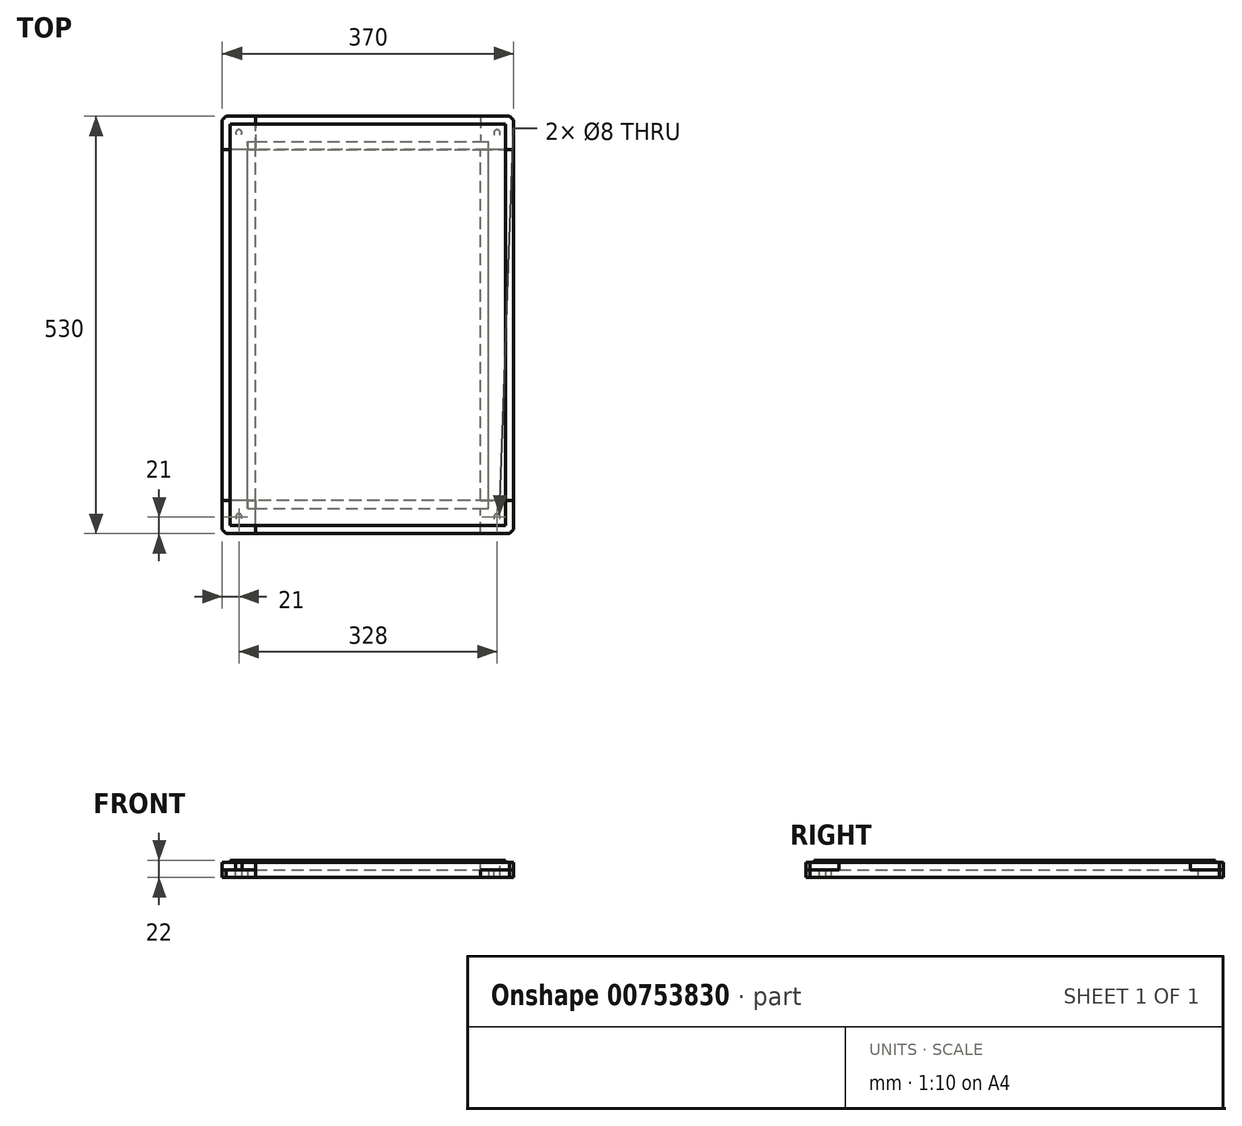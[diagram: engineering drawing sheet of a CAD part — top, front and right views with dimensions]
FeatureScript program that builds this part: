
annotation { "Feature Type Name" : "Feature", "Feature Type Description" : "" }
export const myFeature = defineFeature(function(context is Context, id is Id, definition is map)
    precondition{}
    {
        {
            assignVariable(context, id + "F0", {"name" : "Glass_Thickness", "anyValue" : 3});
        }
        {
            assignVariable(context, id + "F1", {"name" : "Frame_Thickness", "anyValue" : 19});
        }
        {
            assignVariable(context, id + "F2", {"name" : "Rebate_Depth", "anyValue" : 10});
        }
        {
            var Q0;
            Q0=qCreatedBy(makeId("Top.planeOp"),FACE);
            var sketch = newSketch(context, id + "F3", { "sketchPlane" : qUnion([Q0])});
            skLineSegment(sketch, "E0.bottom", {"start": v(-175, 255) * mm, "end": v(175, 255) * mm});
            skLineSegment(sketch, "E0.top", {"start": v(-175, -255) * mm, "end": v(175, -255) * mm});
            skLineSegment(sketch, "E0.left", {"start": v(-175, 255) * mm, "end": v(-175, -255) * mm});
            skLineSegment(sketch, "E0.right", {"start": v(175, 255) * mm, "end": v(175, -255) * mm});
            skSolve(sketch);
        }
        {
            var Q0;
            Q0=makeQuery(id+"F3.imprint","IMPRINT",FACE,{"disambiguationData":[TD([[makeQuery(id+"F3.imprint","IMPRINT",EDGE,{"derivedFrom":sQuery(id+"F3.wireOp",EDGE,"E0.bottom")}),-1.0]])]});
            extrude(context, id + "F4", {"entities" : qUnion([Q0]), "depth" : (getVariable(context, 'Glass_Thickness')) * mm, "offsetDistance" : 25 * mm});
        }
        {
            var Q0;
            Q0=makeQuery(id+"F4.opExtrude","CAP_FACE",FACE,{"disambiguationData":[OSD([sQuery(id+"F3.wireOp",EDGE,"E0.bottom"),sQuery(id+"F3.wireOp",EDGE,"E0.top"),sQuery(id+"F3.wireOp",EDGE,"E0.left"),sQuery(id+"F3.wireOp",EDGE,"E0.right")])],"isStart":true});
            var sketch = newSketch(context, id + "F5", { "sketchPlane" : qUnion([Q0])});
            skLineSegment(sketch, "E1.bottom", {"start": v(185, -265) * mm, "end": v(-185, -265) * mm});
            skLineSegment(sketch, "E1.top", {"start": v(185, -223) * mm, "end": v(-185, -223) * mm});
            skLineSegment(sketch, "E1.left", {"start": v(185, -265) * mm, "end": v(185, -223) * mm});
            skLineSegment(sketch, "E1.right", {"start": v(-185, -265) * mm, "end": v(-185, -223) * mm});
            skCircle(sketch, "E2", {"center": v(-164, -244) * mm, "radius": 4 * mm});
            skCircle(sketch, "E3.MirrorC", {"center": v(164, -244) * mm, "radius": 4 * mm});
            skSolve(sketch);
        }
        {
            var Q0;
            Q0=makeQuery(id+"F5.imprint","IMPRINT",FACE,{"disambiguationData":[TD([[makeQuery(id+"F5.imprint","IMPRINT",EDGE,{"derivedFrom":sQuery(id+"F5.wireOp",EDGE,"E1.bottom")}),-1.0]])]});
            var Q1;
            {var subQ1=makeQuery(id+"F4.opExtrude","CAP_EDGE",EDGE,{"disambiguationData":[OSD([sQuery(id+"F3.wireOp",EDGE,"E0.right")])],"isStart":true});var subQ5=sQuery(id+"F5.wireOp",EDGE,"E1.top");var subQ6=makeQuery(id+"F5.imprint","INTERSECT",VERTEX,{"derivedFrom":[subQ1,subQ5]});Q1=makeQuery(id+"F5.imprint","IMPRINT",FACE,{"disambiguationData":[TD([[makeQuery(id+"F5.imprint","IMPRINT",EDGE,{"disambiguationData":[TD([[subQ6,-1.0]])],"derivedFrom":subQ5}),1.0]])]});}
            var Q2;
            {var subQ0=sQuery(id+"F5.wireOp",EDGE,"E3.MirrorC");var subQ1=makeQuery(id+"F4.opExtrude","CAP_EDGE",EDGE,{"disambiguationData":[OSD([sQuery(id+"F3.wireOp",EDGE,"E0.bottom")])],"isStart":true});var subQ2=makeQuery(id+"F5.imprint","INTERSECT",VERTEX,{"derivedFrom":[subQ1,subQ0]});Q2=makeQuery(id+"F5.imprint","IMPRINT",FACE,{"disambiguationData":[TD([[makeQuery(id+"F5.imprint","IMPRINT",EDGE,{"disambiguationData":[TD([[subQ2,1.0]])],"derivedFrom":subQ0}),1.0]])]});}
            var Q3;
            {var subQ0=sQuery(id+"F5.wireOp",EDGE,"E2");var subQ1=makeQuery(id+"F4.opExtrude","CAP_EDGE",EDGE,{"disambiguationData":[OSD([sQuery(id+"F3.wireOp",EDGE,"E0.bottom")])],"isStart":true});var subQ2=makeQuery(id+"F5.imprint","INTERSECT",VERTEX,{"derivedFrom":[subQ1,subQ0]});Q3=makeQuery(id+"F5.imprint","IMPRINT",FACE,{"disambiguationData":[TD([[makeQuery(id+"F5.imprint","IMPRINT",EDGE,{"disambiguationData":[TD([[subQ2,1.0]])],"derivedFrom":subQ0}),-1.0]])]});}
            extrude(context, id + "F6", {"entities" : qUnion([Q0, Q1, Q2, Q3]), "depth" : (getVariable(context, 'Frame_Thickness')) * mm, "offsetDistance" : 25 * mm});
        }
        {
            var Q0;
            Q0=makeQuery(id+"F6.opExtrude","CAP_FACE",FACE,{"disambiguationData":[OSD([sQuery(id+"F5.wireOp",EDGE,"E1.bottom"),sQuery(id+"F5.wireOp",EDGE,"E1.top"),sQuery(id+"F5.wireOp",EDGE,"E1.left"),sQuery(id+"F5.wireOp",EDGE,"E1.right"),sQuery(id+"F5.wireOp",EDGE,"E2"),sQuery(id+"F5.wireOp",EDGE,"E3.MirrorC")])],"isStart":false});
            var sketch = newSketch(context, id + "F7", { "sketchPlane" : qUnion([Q0])});
            skLineSegment(sketch, "E4", {"start": v(143, -265) * mm, "end": v(143, -223) * mm});
            skLineSegment(sketch, "E5.MirrorCS", {"start": v(-143, -265) * mm, "end": v(-143, -223) * mm});
            skSolve(sketch);
        }
        {
            var Q0;
            {var subQ2=sQuery(id+"F7.wireOp",EDGE,"E5.MirrorCS");Q0=makeQuery(id+"F7.imprint","IMPRINT",FACE,{"disambiguationData":[TD([[makeQuery(id+"F7.imprint","IMPRINT",EDGE,{"derivedFrom":subQ2}),1.0]])]});}
            var Q1;
            {var subQ2=sQuery(id+"F7.wireOp",EDGE,"E4");Q1=makeQuery(id+"F7.imprint","IMPRINT",FACE,{"disambiguationData":[TD([[makeQuery(id+"F7.imprint","IMPRINT",EDGE,{"derivedFrom":subQ2}),-1.0]])]});}
            extrude(context, id + "F8", {"entities" : qUnion([Q0, Q1]), "operationType" : NewBodyOperationType.REMOVE, "oppositeDirection" : true, "depth" : (getVariable(context, 'Frame_Thickness') / 2) * mm, "offsetDistance" : 25 * mm});
        }
        {
            var Q0;
            Q0=makeQuery(id+"F6.opExtrude","SWEPT_EDGE",EDGE,{"disambiguationData":[OSD([sQuery(id+"F5.wireOp",EDGE,"E1.bottom"),sQuery(id+"F5.wireOp",EDGE,"E1.right")])]});
            var Q1;
            Q1=makeQuery(id+"F6.opExtrude","SWEPT_EDGE",EDGE,{"disambiguationData":[OSD([sQuery(id+"F5.wireOp",EDGE,"E1.bottom"),sQuery(id+"F5.wireOp",EDGE,"E1.left")])]});
            chamfer(context, id + "F9", {"entities" : qUnion([Q0, Q1]), "width" : 5 * mm, "tangentPropagation" : true});
        }
        {
            var Q0;
            Q0=makeQuery(id+"F6.opExtrude","SWEPT_BODY",BODY,{"disambiguationData":[OSD([sQuery(id+"F5.wireOp",EDGE,"E1.bottom"),sQuery(id+"F5.wireOp",EDGE,"E1.top"),sQuery(id+"F5.wireOp",EDGE,"E1.left"),sQuery(id+"F5.wireOp",EDGE,"E1.right"),sQuery(id+"F5.wireOp",EDGE,"E2"),sQuery(id+"F5.wireOp",EDGE,"E3.MirrorC")])]});
            var Q1;
            Q1=qCreatedBy(makeId("Front.planeOp"),FACE);
            mirror(context, id + "F10", {"operationType" : NewBodyOperationType.ADD, "entities" : qUnion([Q0]), "mirrorPlane" : qUnion([Q1])});
        }
        {
            var Q0;
            Q0=makeQuery(id+"F4.opExtrude","CAP_FACE",FACE,{"disambiguationData":[OSD([sQuery(id+"F3.wireOp",EDGE,"E0.bottom"),sQuery(id+"F3.wireOp",EDGE,"E0.top"),sQuery(id+"F3.wireOp",EDGE,"E0.left"),sQuery(id+"F3.wireOp",EDGE,"E0.right")])],"isStart":true});
            var sketch = newSketch(context, id + "F11", { "sketchPlane" : qUnion([Q0])});
            skLineSegment(sketch, "E6.bottom", {"start": v(-185, 265) * mm, "end": v(-143, 265) * mm});
            skLineSegment(sketch, "E6.top", {"start": v(-185, -265) * mm, "end": v(-143, -265) * mm});
            skLineSegment(sketch, "E6.left", {"start": v(-185, 265) * mm, "end": v(-185, -265) * mm});
            skLineSegment(sketch, "E6.right", {"start": v(-143, 265) * mm, "end": v(-143, -265) * mm});
            skCircle(sketch, "E7", {"center": v(-164, 244) * mm, "radius": 4 * mm});
            skCircle(sketch, "E8.MirrorC", {"center": v(-164, -244) * mm, "radius": 4 * mm});
            skSolve(sketch);
        }
        {
            var Q0;
            {var subQ13=sQuery(id+"F11.wireOp",EDGE,"E6.bottom");Q0=makeQuery(id+"F11.imprint","IMPRINT",FACE,{"disambiguationData":[TD([[makeQuery(id+"F11.imprint","IMPRINT",EDGE,{"derivedFrom":subQ13}),-1.0]])]});}
            var Q1;
            {var subQ0=sQuery(id+"F11.wireOp",EDGE,"E8.MirrorC");var subQ1=makeQuery(id+"F4.opExtrude","CAP_EDGE",EDGE,{"disambiguationData":[OSD([sQuery(id+"F3.wireOp",EDGE,"E0.bottom")])],"isStart":true});var subQ2=makeQuery(id+"F11.imprint","INTERSECT",VERTEX,{"derivedFrom":[subQ1,subQ0]});Q1=makeQuery(id+"F11.imprint","IMPRINT",FACE,{"disambiguationData":[TD([[makeQuery(id+"F11.imprint","IMPRINT",EDGE,{"disambiguationData":[TD([[subQ2,-1.0]])],"derivedFrom":subQ0}),1.0]])]});}
            var Q2;
            {var subQ0=sQuery(id+"F11.wireOp",EDGE,"E6.right");var subQ6=makeQuery(id+"F4.opExtrude","CAP_EDGE",EDGE,{"disambiguationData":[OSD([sQuery(id+"F3.wireOp",EDGE,"E0.top")])],"isStart":true});var subQ11=makeQuery(id+"F11.imprint","INTERSECT",VERTEX,{"derivedFrom":[subQ6,subQ0]});Q2=makeQuery(id+"F11.imprint","IMPRINT",FACE,{"disambiguationData":[TD([[makeQuery(id+"F11.imprint","IMPRINT",EDGE,{"disambiguationData":[TD([[subQ11,-1.0]])],"derivedFrom":subQ0}),-1.0]])]});}
            var Q3;
            {var subQ0=sQuery(id+"F11.wireOp",EDGE,"E7");var subQ1=makeQuery(id+"F4.opExtrude","CAP_EDGE",EDGE,{"disambiguationData":[OSD([sQuery(id+"F3.wireOp",EDGE,"E0.top")])],"isStart":true});var subQ2=makeQuery(id+"F11.imprint","INTERSECT",VERTEX,{"derivedFrom":[subQ1,subQ0]});Q3=makeQuery(id+"F11.imprint","IMPRINT",FACE,{"disambiguationData":[TD([[makeQuery(id+"F11.imprint","IMPRINT",EDGE,{"disambiguationData":[TD([[subQ2,-1.0]])],"derivedFrom":subQ0}),-1.0]])]});}
            extrude(context, id + "F12", {"entities" : qUnion([Q0, Q1, Q2, Q3]), "depth" : (getVariable(context, 'Frame_Thickness')) * mm, "offsetDistance" : 25 * mm});
        }
        {
            var Q0;
            Q0=makeQuery(id+"F12.opExtrude","CAP_FACE",FACE,{"disambiguationData":[OSD([sQuery(id+"F11.wireOp",EDGE,"E6.bottom"),sQuery(id+"F11.wireOp",EDGE,"E6.top"),sQuery(id+"F11.wireOp",EDGE,"E6.left"),sQuery(id+"F11.wireOp",EDGE,"E6.right"),sQuery(id+"F11.wireOp",EDGE,"E7"),sQuery(id+"F11.wireOp",EDGE,"E8.MirrorC")])],"isStart":true});
            var sketch = newSketch(context, id + "F13", { "sketchPlane" : qUnion([Q0])});
            skLineSegment(sketch, "E9", {"start": v(-143, -223) * mm, "end": v(-185, -223) * mm});
            skLineSegment(sketch, "E10.MirrorCS", {"start": v(-143, 223) * mm, "end": v(-185, 223) * mm});
            skSolve(sketch);
        }
        {
            var Q0;
            {var subQ2=sQuery(id+"F13.wireOp",EDGE,"E10.MirrorCS");Q0=makeQuery(id+"F13.imprint","IMPRINT",FACE,{"disambiguationData":[TD([[makeQuery(id+"F13.imprint","IMPRINT",EDGE,{"derivedFrom":subQ2}),-1.0]])]});}
            var Q1;
            {var subQ2=sQuery(id+"F13.wireOp",EDGE,"E9");Q1=makeQuery(id+"F13.imprint","IMPRINT",FACE,{"disambiguationData":[TD([[makeQuery(id+"F13.imprint","IMPRINT",EDGE,{"derivedFrom":subQ2}),1.0]])]});}
            extrude(context, id + "F14", {"entities" : qUnion([Q0, Q1]), "operationType" : NewBodyOperationType.REMOVE, "oppositeDirection" : true, "depth" : (getVariable(context, 'Frame_Thickness') / 2) * mm, "offsetDistance" : 25 * mm});
        }
        {
            var Q0;
            Q0=makeQuery(id+"F12.opExtrude","SWEPT_EDGE",EDGE,{"disambiguationData":[OSD([sQuery(id+"F11.wireOp",EDGE,"E6.bottom"),sQuery(id+"F11.wireOp",EDGE,"E6.left")])]});
            var Q1;
            Q1=makeQuery(id+"F12.opExtrude","SWEPT_EDGE",EDGE,{"disambiguationData":[OSD([sQuery(id+"F11.wireOp",EDGE,"E6.top"),sQuery(id+"F11.wireOp",EDGE,"E6.left")])]});
            chamfer(context, id + "F15", {"entities" : qUnion([Q0, Q1]), "width" : 5 * mm, "tangentPropagation" : true});
        }
        {
            var Q0;
            Q0=makeQuery(id+"F12.opExtrude","SWEPT_BODY",BODY,{"disambiguationData":[OSD([sQuery(id+"F11.wireOp",EDGE,"E6.bottom"),sQuery(id+"F11.wireOp",EDGE,"E6.top"),sQuery(id+"F11.wireOp",EDGE,"E6.left"),sQuery(id+"F11.wireOp",EDGE,"E6.right"),sQuery(id+"F11.wireOp",EDGE,"E7"),sQuery(id+"F11.wireOp",EDGE,"E8.MirrorC")])]});
            var Q1;
            Q1=qCreatedBy(makeId("Right.planeOp"),FACE);
            mirror(context, id + "F16", {"entities" : qUnion([Q0]), "mirrorPlane" : qUnion([Q1])});
        }
        {
            var Q0;
            Q0=makeQuery(id+"F4.opExtrude","CAP_FACE",FACE,{"disambiguationData":[OSD([sQuery(id+"F3.wireOp",EDGE,"E0.bottom"),sQuery(id+"F3.wireOp",EDGE,"E0.top"),sQuery(id+"F3.wireOp",EDGE,"E0.left"),sQuery(id+"F3.wireOp",EDGE,"E0.right")])],"isStart":true});
            var sketch = newSketch(context, id + "F17", { "sketchPlane" : qUnion([Q0])});
            skCircle(sketch, "E11.0", {"center": v(-164, 244) * mm, "radius": 4 * mm});
            skCircle(sketch, "E12.0", {"center": v(164, 244) * mm, "radius": 4 * mm});
            skCircle(sketch, "E13.0", {"center": v(164, -244) * mm, "radius": 4 * mm});
            skCircle(sketch, "E14.0", {"center": v(-164, -244) * mm, "radius": 4 * mm});
            skSolve(sketch);
        }
        {
            var Q0;
            {var subQ0=sQuery(id+"F17.wireOp",EDGE,"E11.0");var subQ1=makeQuery(id+"F17.imprint","INTERSECT",VERTEX,{"derivedFrom":[makeQuery(id+"F4.opExtrude","CAP_EDGE",EDGE,{"disambiguationData":[OSD([sQuery(id+"F3.wireOp",EDGE,"E0.top")])],"isStart":true}),subQ0]});Q0=makeQuery(id+"F17.imprint","IMPRINT",FACE,{"disambiguationData":[TD([[makeQuery(id+"F17.imprint","IMPRINT",EDGE,{"disambiguationData":[TD([[subQ1,-1.0]])],"derivedFrom":subQ0}),1.0]])]});}
            extrude(context, id + "F18", {"entities" : qUnion([Q0]), "depth" : (getVariable(context, 'Frame_Thickness')) * mm, "offsetDistance" : 25 * mm});
        }
        {
            var Q0;
            Q0=makeQuery(id+"F18.opExtrude","SWEPT_BODY",BODY,{"disambiguationData":[OSD([sQuery(id+"F17.wireOp",EDGE,"E11.0")])]});
            var Q1;
            Q1=qCreatedBy(makeId("Right.planeOp"),FACE);
            mirror(context, id + "F19", {"entities" : qUnion([Q0]), "mirrorPlane" : qUnion([Q1])});
        }
        {
            var Q0;
            Q0=makeQuery(id+"F18.opExtrude","SWEPT_BODY",BODY,{"disambiguationData":[OSD([sQuery(id+"F17.wireOp",EDGE,"E11.0")])]});
            var Q1;
            Q1=makeQuery(id+"F19.opPattern","COPY",BODY,{"derivedFrom":makeQuery(id+"F18.opExtrude","SWEPT_BODY",BODY,{"disambiguationData":[OSD([sQuery(id+"F17.wireOp",EDGE,"E11.0")])]}),"instanceName":"1"});
            var Q2;
            Q2=qCreatedBy(makeId("Front.planeOp"),FACE);
            mirror(context, id + "F20", {"entities" : qUnion([Q0, Q1]), "mirrorPlane" : qUnion([Q2])});
        }
        {
            var Q0;
            Q0=qCreatedBy(makeId("Top.planeOp"),FACE);
            cPlane(context, id + "F21", {"entities" : qUnion([Q0]), "cplaneType" : CPlaneType.OFFSET, "offset" : (getVariable(context, 'Frame_Thickness')) * mm, "oppositeDirection" : true, "width" : 150 * mm, "height" : 150 * mm});
        }
        {
            var Q0;
            Q0=qCreatedBy(id+"F21.planeOp",FACE);
            var sketch = newSketch(context, id + "F22", { "sketchPlane" : qUnion([Q0])});
            skLineSegment(sketch, "E15.bottom", {"start": v(-185, -265) * mm, "end": v(185, -265) * mm});
            skLineSegment(sketch, "E15.top", {"start": v(-185, 265) * mm, "end": v(185, 265) * mm});
            skLineSegment(sketch, "E15.left", {"start": v(-185, -265) * mm, "end": v(-185, 265) * mm});
            skLineSegment(sketch, "E15.right", {"start": v(185, -265) * mm, "end": v(185, 265) * mm});
            skLineSegment(sketch, "E16.0", {"start": v(-143, -223) * mm, "end": v(143, -223) * mm});
            skLineSegment(sketch, "E16.1", {"start": v(-143, -223) * mm, "end": v(-143, 223) * mm});
            skLineSegment(sketch, "E16.2", {"start": v(-143, 223) * mm, "end": v(143, 223) * mm});
            skLineSegment(sketch, "E16.3", {"start": v(143, -223) * mm, "end": v(143, 223) * mm});
            skLineSegment(sketch, "E17.0", {"start": v(-153, -233) * mm, "end": v(153, -233) * mm});
            skLineSegment(sketch, "E17.1", {"start": v(-153, -233) * mm, "end": v(-153, 233) * mm});
            skLineSegment(sketch, "E17.2", {"start": v(-153, 233) * mm, "end": v(153, 233) * mm});
            skLineSegment(sketch, "E17.3", {"start": v(153, -233) * mm, "end": v(153, 233) * mm});
            skSolve(sketch);
        }
        {
            var Q0;
            Q0=makeQuery(id+"F22.imprint","IMPRINT",FACE,{"disambiguationData":[TD([[makeQuery(id+"F22.imprint","IMPRINT",EDGE,{"derivedFrom":sQuery(id+"F22.wireOp",EDGE,"E16.0")}),-1.0]])]});
            extrude(context, id + "F23", {"entities" : qUnion([Q0]), "operationType" : NewBodyOperationType.REMOVE, "depth" : (getVariable(context, 'Rebate_Depth')) * mm, "offsetDistance" : 25 * mm});
        }
    });
